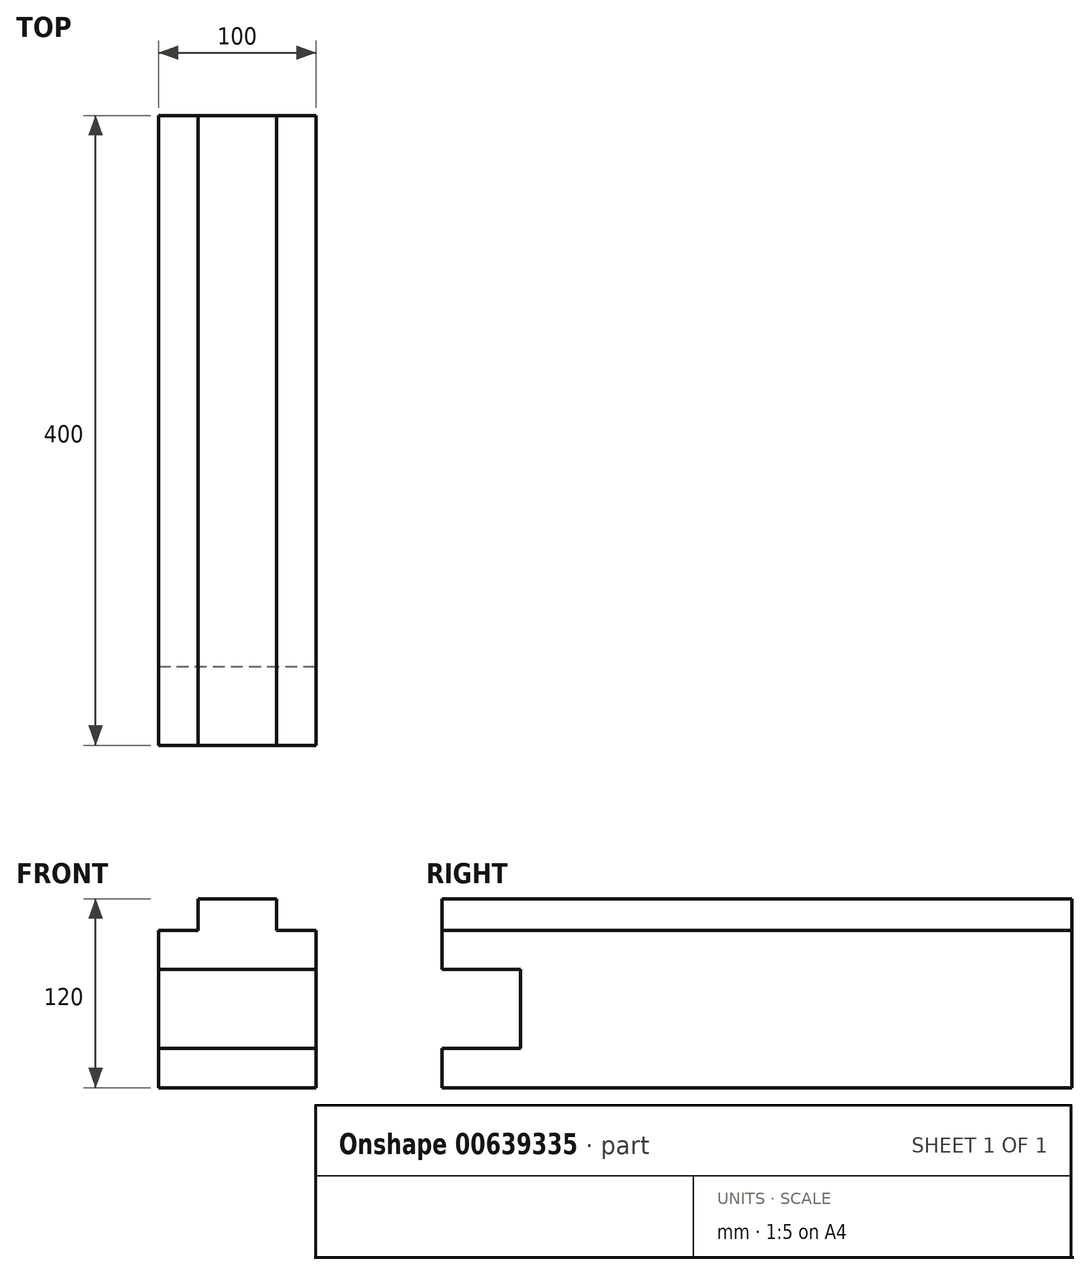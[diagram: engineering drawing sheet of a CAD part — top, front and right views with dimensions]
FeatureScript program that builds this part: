
annotation { "Feature Type Name" : "Feature", "Feature Type Description" : "" }
export const myFeature = defineFeature(function(context is Context, id is Id, definition is map)
    precondition{}
    {
        {
            var Q0;
            Q0=qCreatedBy(makeId("Right.planeOp"),FACE);
            var sketch = newSketch(context, id + "F0", { "sketchPlane" : qUnion([Q0])});
            skLineSegment(sketch, "E0.bottom", {"start": v(-206.6, 58.23) * mm, "end": v(193.4, 58.23) * mm});
            skLineSegment(sketch, "E0.top", {"start": v(-206.6, -41.77) * mm, "end": v(193.4, -41.77) * mm});
            skLineSegment(sketch, "E0.left", {"start": v(-206.6, 58.23) * mm, "end": v(-206.6, -41.77) * mm});
            skLineSegment(sketch, "E0.right", {"start": v(193.4, 58.23) * mm, "end": v(193.4, -41.77) * mm});
            skSolve(sketch);
        }
        {
            var Q0;
            Q0 = qSketchRegion(id + "F0", true);
            extrude(context, id + "F1", {"entities" : qUnion([Q0]), "depth" : 100 * mm, "offsetDistance" : 25 * mm});
        }
        {
            var Q0;
            Q0=makeQuery(id+"F1.opExtrude","CAP_FACE",FACE,{"disambiguationData":[OSD([sQuery(id+"F0.wireOp",EDGE,"E0.bottom"),sQuery(id+"F0.wireOp",EDGE,"E0.top"),sQuery(id+"F0.wireOp",EDGE,"E0.left"),sQuery(id+"F0.wireOp",EDGE,"E0.right")])],"isStart":false});
            var sketch = newSketch(context, id + "F2", { "sketchPlane" : qUnion([Q0])});
            skLineSegment(sketch, "E1.bottom", {"start": v(-206.6, 33.23) * mm, "end": v(-156.6, 33.23) * mm});
            skLineSegment(sketch, "E1.top", {"start": v(-206.6, -16.77) * mm, "end": v(-156.6, -16.77) * mm});
            skLineSegment(sketch, "E1.left", {"start": v(-206.6, 33.23) * mm, "end": v(-206.6, -16.77) * mm});
            skLineSegment(sketch, "E1.right", {"start": v(-156.6, 33.23) * mm, "end": v(-156.6, -16.77) * mm});
            skSolve(sketch);
        }
        {
            var Q0;
            Q0 = qSketchRegion(id + "F2", true);
            extrude(context, id + "F3", {"entities" : qUnion([Q0]), "operationType" : NewBodyOperationType.REMOVE, "oppositeDirection" : true, "depth" : 100 * mm, "offsetDistance" : 25 * mm});
        }
        {
            var Q0;
            Q0=makeQuery(id+"F1.opExtrude","SWEPT_FACE",FACE,{"disambiguationData":[OSD([sQuery(id+"F0.wireOp",EDGE,"E0.bottom")])]});
            var sketch = newSketch(context, id + "F4", { "sketchPlane" : qUnion([Q0])});
            skLineSegment(sketch, "E2.bottom", {"start": v(25, 193.4) * mm, "end": v(75, 193.4) * mm});
            skLineSegment(sketch, "E2.top", {"start": v(25, -206.6) * mm, "end": v(75, -206.6) * mm});
            skLineSegment(sketch, "E2.left", {"start": v(25, 193.4) * mm, "end": v(25, -206.6) * mm});
            skLineSegment(sketch, "E2.right", {"start": v(75, 193.4) * mm, "end": v(75, -206.6) * mm});
            skSolve(sketch);
        }
        {
            var Q0;
            Q0 = qSketchRegion(id + "F4", true);
            extrude(context, id + "F5", {"entities" : qUnion([Q0]), "operationType" : NewBodyOperationType.ADD, "depth" : 20 * mm, "offsetDistance" : 25 * mm});
        }
    });
